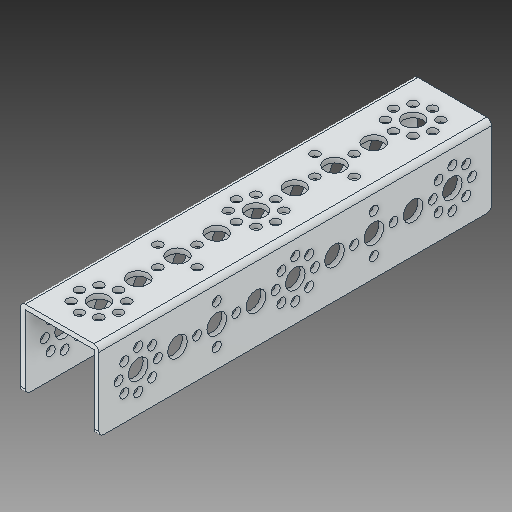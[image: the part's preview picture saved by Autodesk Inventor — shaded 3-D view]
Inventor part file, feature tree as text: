
AUTODESK INVENTOR PART (.ipt)
format: ipt  version: 2018 (Build 220112000, 112)  size: 304,128 bytes
history: native  units: in
note: dims shown in document units (in); Inventor stores cm internally (conversion verified against a paired STEP export)
features: fillet x1
ambient origin geometry x8: Origin, YZ Plane, XZ Plane, XY Plane, X Axis, Y Axis, Z Axis, Center Point
bodies: Solid1 (feature_tree)
feature tree (1):
  fillet  "Fillet1"  [1 undecoded]
note: 1 required parameter value undecoded (feature->parameter linkage not recoverable at this tier; creation-order binding heuristic only, values carry confidence <= 0.55)
